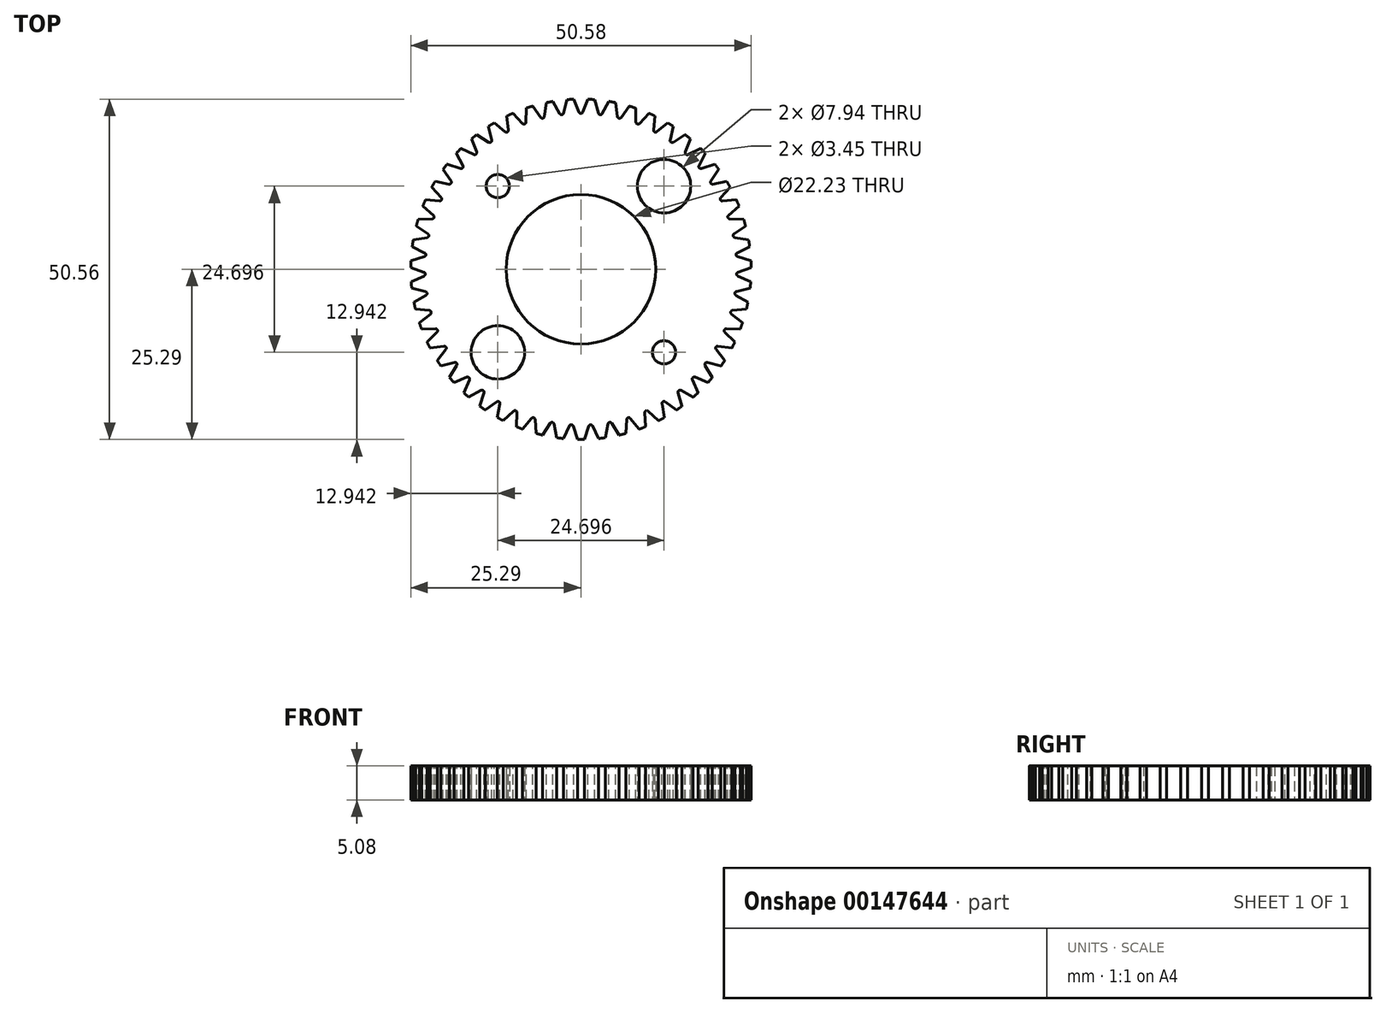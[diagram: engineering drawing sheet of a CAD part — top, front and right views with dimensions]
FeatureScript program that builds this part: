
annotation { "Feature Type Name" : "Feature", "Feature Type Description" : "" }
export const myFeature = defineFeature(function(context is Context, id is Id, definition is map)
    precondition{}
    {
        {
            var Q0;
            Q0=qCreatedBy(makeId("Top.planeOp"),FACE);
            var sketch = newSketch(context, id + "F0", { "sketchPlane" : qUnion([Q0])});
            skCircle(sketch, "E0", {"center": v(0, 0) * mm, "radius": 25.3 * mm});
            skCircle(sketch, "E1", {"center": v(0, 0) * mm, "radius": 11.9 * mm, "construction": true});
            skLineSegment(sketch, "E2.bottom", {"start": v(12.35, -12.35) * mm, "end": v(-12.35, -12.35) * mm, "construction": true});
            skLineSegment(sketch, "E2.top", {"start": v(12.35, 12.35) * mm, "end": v(-12.35, 12.35) * mm, "construction": true});
            skLineSegment(sketch, "E2.left", {"start": v(12.35, -12.35) * mm, "end": v(12.35, 12.35) * mm, "construction": true});
            skLineSegment(sketch, "E2.right", {"start": v(-12.35, -12.35) * mm, "end": v(-12.35, 12.35) * mm, "construction": true});
            skCircle(sketch, "E3", {"center": v(12.35, -12.35) * mm, "radius": 5.56 * mm, "construction": true});
            skCircle(sketch, "E4", {"center": v(12.35, 12.35) * mm, "radius": 3.97 * mm});
            skCircle(sketch, "E5", {"center": v(-12.35, -12.35) * mm, "radius": 3.97 * mm});
            skCircle(sketch, "E6", {"center": v(12.35, -12.35) * mm, "radius": 1.73 * mm});
            skCircle(sketch, "E7", {"center": v(-12.35, 12.35) * mm, "radius": 1.73 * mm});
            skCircle(sketch, "E8", {"center": v(0, 0) * mm, "radius": 11.11 * mm});
            skSolve(sketch);
        }
        {
            var Q0;
            Q0=qSketchRegion(id+"F0",true);
            extrude(context, id + "F1", {"entities" : qUnion([Q0]), "depth" : 5.08 * mm});
        }
        {
            var Q0;
            Q0=makeQuery(id+"F1.opExtrude","CAP_FACE",FACE,{"disambiguationData":[OSD([sQuery(id+"F0.wireOp",EDGE,"E0")])],"isStart":false});
            var sketch = newSketch(context, id + "F2", { "sketchPlane" : qUnion([Q0])});
            skLineSegment(sketch, "E9", {"start": v(0, 0) * mm, "end": v(0, 25.3) * mm});
            skArc(sketch, "E10", {"start": v(1.05, 25.27) * mm, "mid": v(0, 25.3) * mm, "end": v(-1.05, 25.27) * mm});
            skLineSegment(sketch, "E11", {"start": v(-1.05, 25.27) * mm, "end": v(-0.28, 23.33) * mm});
            skLineSegment(sketch, "E12", {"start": v(1.05, 25.27) * mm, "end": v(0.28, 23.33) * mm});
            skArc(sketch, "E13", {"start": v(-0.28, 23.33) * mm, "mid": v(0, 23.14) * mm, "end": v(0.28, 23.33) * mm});
            skLineSegment(sketch, "E14", {"start": v(0, 0) * mm, "end": v(0.7, 25.28) * mm, "construction": true});
            skPoint(sketch, "E15", {"position": v(0.67, 24.3) * mm});
            skSolve(sketch);
        }
        {
            var Q0;
            Q0=qSketchRegion(id+"F2",true);
            var Q1;
            Q1=makeQuery(id+"F1.opExtrude","CAP_FACE",FACE,{"disambiguationData":[OSD([sQuery(id+"F0.wireOp",EDGE,"E0")])],"isStart":true});
            extrude(context, id + "F3", {"entities" : qUnion([Q0]), "operationType" : NewBodyOperationType.REMOVE, "endBound" : BoundingType.UP_TO_SURFACE, "oppositeDirection" : true, "endBoundEntityFace" : qUnion([Q1]), "depth" : 25.4 * mm});
        }
        {
            var Q0;
            Q0=makeQuery(id+"F3.boolean.opBoolean","COPY",FACE,{"derivedFrom":makeQuery(id+"F3.opExtrude","SWEPT_FACE",FACE,{"disambiguationData":[OSD([sQuery(id+"F2.wireOp",EDGE,"E12")])]})});
            var Q1;
            Q1=makeQuery(id+"F3.boolean.opBoolean","COPY",FACE,{"derivedFrom":makeQuery(id+"F3.opExtrude","SWEPT_FACE",FACE,{"disambiguationData":[OSD([sQuery(id+"F2.wireOp",EDGE,"E13")])]})});
            var Q2;
            Q2=makeQuery(id+"F3.boolean.opBoolean","COPY",FACE,{"derivedFrom":makeQuery(id+"F3.opExtrude","SWEPT_FACE",FACE,{"disambiguationData":[OSD([sQuery(id+"F2.wireOp",EDGE,"E11")])]})});
            var Q3;
            Q3=makeQuery(id+"F1.opExtrude","SWEPT_FACE",FACE,{"disambiguationData":[OSD([sQuery(id+"F0.wireOp",EDGE,"E0")])]});
            circularPattern(context, id + "F4", {"patternType" : PatternType.FACE, "faces" : qUnion([Q0, Q1, Q2]), "axis" : qUnion([Q3]), "angle" : 7.06 * degree, "instanceCount" : 51});
        }
    });
